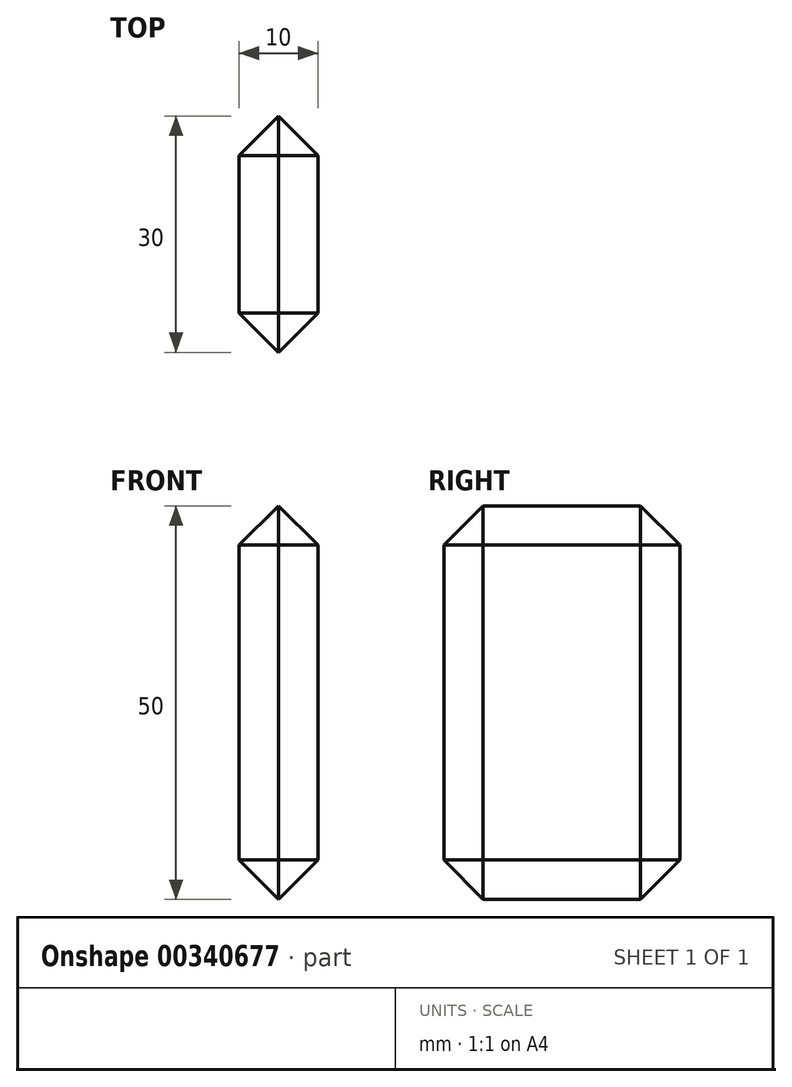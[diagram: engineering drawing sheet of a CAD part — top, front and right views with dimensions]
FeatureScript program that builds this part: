
annotation { "Feature Type Name" : "Feature", "Feature Type Description" : "" }
export const myFeature = defineFeature(function(context is Context, id is Id, definition is map)
    precondition{}
    {
        {
            var Q0;
            Q0=qCreatedBy(makeId("Right.planeOp"),FACE);
            var sketch = newSketch(context, id + "F0", { "sketchPlane" : qUnion([Q0])});
            skLineSegment(sketch, "E0.bottom", {"start": v(-15, 25) * mm, "end": v(15, 25) * mm});
            skLineSegment(sketch, "E0.top", {"start": v(-15, -25) * mm, "end": v(15, -25) * mm});
            skLineSegment(sketch, "E0.left", {"start": v(-15, 25) * mm, "end": v(-15, -25) * mm});
            skLineSegment(sketch, "E0.right", {"start": v(15, 25) * mm, "end": v(15, -25) * mm});
            skPoint(sketch, "E0.middle", {"position": v(0, 0) * mm});
            skSolve(sketch);
        }
        {
            var Q0;
            Q0 = qSketchRegion(id + "F0", true);
            extrude(context, id + "F1", {"entities" : qUnion([Q0]), "depth" : 10 * mm});
        }
        {
            var Q0;
            Q0=makeQuery(id+"F1.opExtrude","SWEPT_FACE",FACE,{"disambiguationData":[OSD([sQuery(id+"F0.wireOp",EDGE,"E0.left")])]});
            var Q1;
            Q1=makeQuery(id+"F1.opExtrude","SWEPT_FACE",FACE,{"disambiguationData":[OSD([sQuery(id+"F0.wireOp",EDGE,"E0.right")])]});
            var Q2;
            Q2=makeQuery(id+"F1.opExtrude","CAP_FACE",FACE,{"disambiguationData":[OSD([sQuery(id+"F0.wireOp",EDGE,"E0.bottom"),sQuery(id+"F0.wireOp",EDGE,"E0.top"),sQuery(id+"F0.wireOp",EDGE,"E0.left"),sQuery(id+"F0.wireOp",EDGE,"E0.right")])],"isStart":false});
            var Q3;
            Q3=makeQuery(id+"F1.opExtrude","CAP_EDGE",EDGE,{"disambiguationData":[OSD([sQuery(id+"F0.wireOp",EDGE,"E0.bottom")])],"isStart":true});
            var Q4;
            Q4=makeQuery(id+"F1.opExtrude","SWEPT_FACE",FACE,{"disambiguationData":[OSD([sQuery(id+"F0.wireOp",EDGE,"E0.bottom")])]});
            var Q5;
            Q5=makeQuery(id+"F1.opExtrude","SWEPT_FACE",FACE,{"disambiguationData":[OSD([sQuery(id+"F0.wireOp",EDGE,"E0.top")])]});
            chamfer(context, id + "F2", {"entities" : qUnion([Q0, Q1, Q2, Q3, Q4, Q5]), "width" : 5 * mm, "tangentPropagation" : true});
        }
    });
